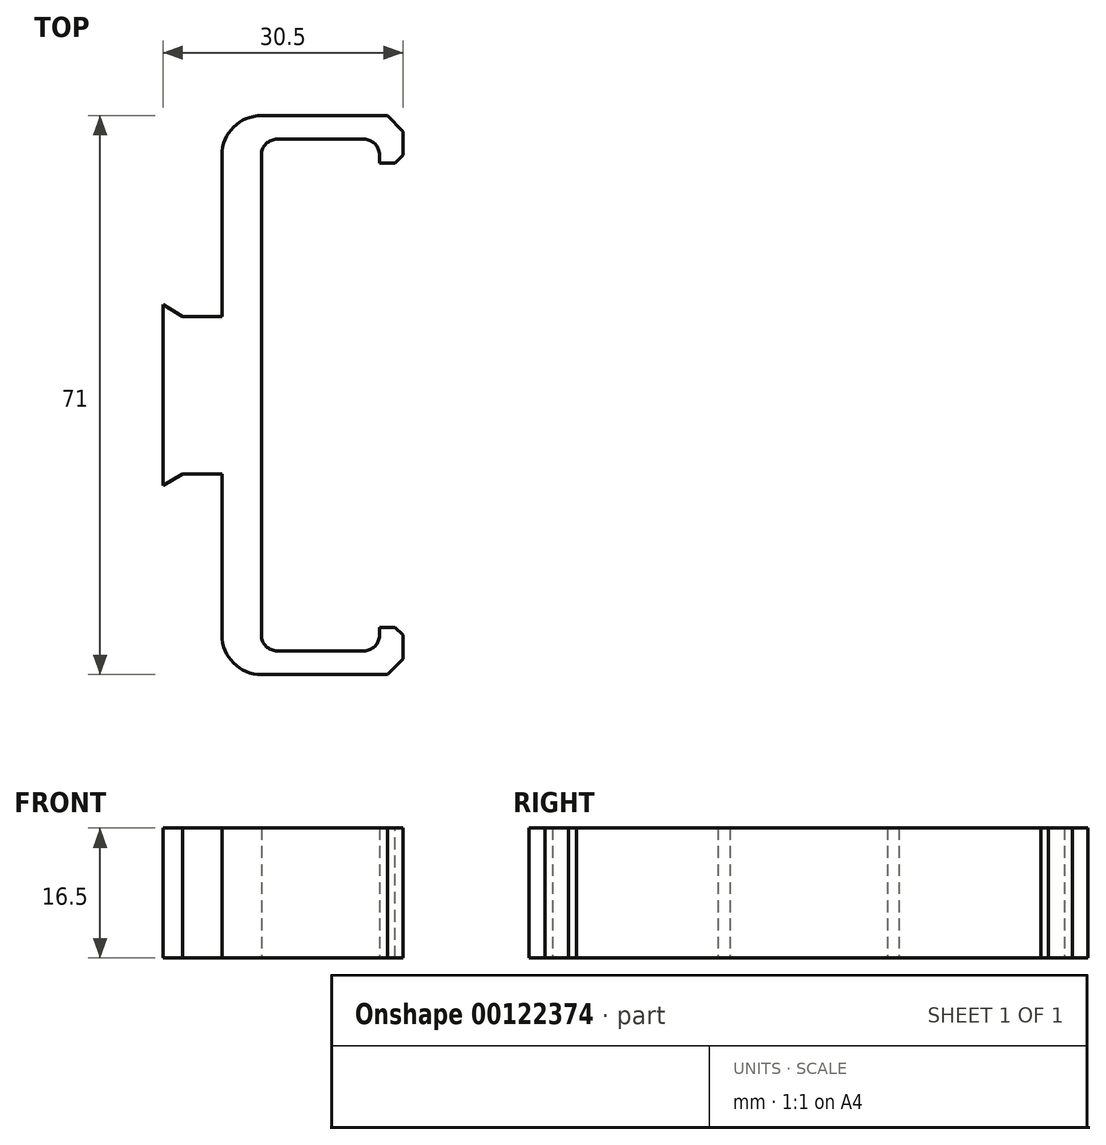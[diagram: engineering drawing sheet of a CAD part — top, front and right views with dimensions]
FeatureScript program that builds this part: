
annotation { "Feature Type Name" : "Feature", "Feature Type Description" : "" }
export const myFeature = defineFeature(function(context is Context, id is Id, definition is map)
    precondition{}
    {
        {
            var Q0;
            Q0=qCreatedBy(makeId("Top.planeOp"),FACE);
            var sketch = newSketch(context, id + "F0", { "sketchPlane" : qUnion([Q0])});
            skLineSegment(sketch, "E0.bottom", {"start": v(0, 35.5) * mm, "end": v(23, 35.5) * mm});
            skLineSegment(sketch, "E0.top", {"start": v(0, -35.5) * mm, "end": v(23, -35.5) * mm});
            skLineSegment(sketch, "E0.left", {"start": v(0, 35.5) * mm, "end": v(0, 10) * mm});
            skLineSegment(sketch, "E0.right", {"start": v(23, 35.5) * mm, "end": v(23, 29.5) * mm});
            skLineSegment(sketch, "E1.bottom", {"start": v(5, 32.5) * mm, "end": v(20, 32.5) * mm});
            skLineSegment(sketch, "E1.top", {"start": v(5, -32.5) * mm, "end": v(20, -32.5) * mm});
            skLineSegment(sketch, "E1.left", {"start": v(5, 32.5) * mm, "end": v(5, -32.5) * mm});
            skLineSegment(sketch, "E1.right", {"start": v(20, 32.5) * mm, "end": v(20, 29.5) * mm});
            skLineSegment(sketch, "E2", {"start": v(20, 29.5) * mm, "end": v(23, 29.5) * mm});
            skLineSegment(sketch, "E3", {"start": v(20, -29.5) * mm, "end": v(23, -29.5) * mm});
            skLineSegment(sketch, "E4.trimOffspring", {"start": v(20, -29.5) * mm, "end": v(20, -32.5) * mm});
            skLineSegment(sketch, "E5.trimOffspring", {"start": v(23, -29.5) * mm, "end": v(23, -35.5) * mm});
            skLineSegment(sketch, "E6.bottom", {"start": v(-5, 10) * mm, "end": v(0, 10) * mm});
            skLineSegment(sketch, "E6.top", {"start": v(-5, -10) * mm, "end": v(0, -10) * mm});
            skLineSegment(sketch, "E6.left", {"start": v(-5, 10) * mm, "end": v(-5, -10) * mm});
            skLineSegment(sketch, "E7.trimOffspring", {"start": v(0, -10) * mm, "end": v(0, -35.5) * mm});
            skSolve(sketch);
        }
        {
            var Q0;
            Q0=makeQuery(id+"F0.imprint","IMPRINT",FACE,{"disambiguationData":[TD([[makeQuery(id+"F0.imprint","IMPRINT",EDGE,{"derivedFrom":sQuery(id+"F0.wireOp",EDGE,"E0.bottom")}),-1.0]])]});
            extrude(context, id + "F1", {"entities" : qUnion([Q0]), "depth" : 16.5 * mm});
        }
        {
            var Q0;
            Q0=makeQuery(id+"F1.opExtrude","SWEPT_EDGE",EDGE,{"disambiguationData":[OSD([sQuery(id+"F0.wireOp",EDGE,"E0.top"),sQuery(id+"F0.wireOp",EDGE,"E7.trimOffspring")])]});
            var Q1;
            Q1=makeQuery(id+"F1.opExtrude","SWEPT_EDGE",EDGE,{"disambiguationData":[OSD([sQuery(id+"F0.wireOp",EDGE,"E0.bottom"),sQuery(id+"F0.wireOp",EDGE,"E0.left")])]});
            fillet(context, id + "F2", {"entities" : qUnion([Q0, Q1]), "radius" : 5 * mm, "tangentPropagation" : true, "allowEdgeOverflow" : false});
        }
        {
            var Q0;
            Q0=makeQuery(id+"F1.opExtrude","SWEPT_EDGE",EDGE,{"disambiguationData":[OSD([sQuery(id+"F0.wireOp",EDGE,"E1.bottom"),sQuery(id+"F0.wireOp",EDGE,"E1.left")])]});
            var Q1;
            Q1=makeQuery(id+"F1.opExtrude","SWEPT_EDGE",EDGE,{"disambiguationData":[OSD([sQuery(id+"F0.wireOp",EDGE,"E1.top"),sQuery(id+"F0.wireOp",EDGE,"E1.left")])]});
            var Q2;
            Q2=makeQuery(id+"F1.opExtrude","SWEPT_EDGE",EDGE,{"disambiguationData":[OSD([sQuery(id+"F0.wireOp",EDGE,"E1.bottom"),sQuery(id+"F0.wireOp",EDGE,"E1.right")])]});
            var Q3;
            Q3=makeQuery(id+"F1.opExtrude","SWEPT_EDGE",EDGE,{"disambiguationData":[OSD([sQuery(id+"F0.wireOp",EDGE,"E1.top"),sQuery(id+"F0.wireOp",EDGE,"E4.trimOffspring")])]});
            fillet(context, id + "F3", {"entities" : qUnion([Q0, Q1, Q2, Q3]), "radius" : 2 * mm, "tangentPropagation" : true, "allowEdgeOverflow" : false});
        }
        {
            var Q0;
            Q0=makeQuery(id+"F1.opExtrude","SWEPT_EDGE",EDGE,{"disambiguationData":[OSD([sQuery(id+"F0.wireOp",EDGE,"E0.right"),sQuery(id+"F0.wireOp",EDGE,"E2")])]});
            var Q1;
            Q1=makeQuery(id+"F1.opExtrude","SWEPT_EDGE",EDGE,{"disambiguationData":[OSD([sQuery(id+"F0.wireOp",EDGE,"E3"),sQuery(id+"F0.wireOp",EDGE,"E5.trimOffspring")])]});
            chamfer(context, id + "F4", {"entities" : qUnion([Q0, Q1]), "width" : 1 * mm, "tangentPropagation" : true});
        }
        {
            var Q0;
            Q0=makeQuery(id+"F1.opExtrude","SWEPT_EDGE",EDGE,{"disambiguationData":[OSD([sQuery(id+"F0.wireOp",EDGE,"E0.bottom"),sQuery(id+"F0.wireOp",EDGE,"E0.right")])]});
            var Q1;
            Q1=makeQuery(id+"F1.opExtrude","SWEPT_EDGE",EDGE,{"disambiguationData":[OSD([sQuery(id+"F0.wireOp",EDGE,"E0.top"),sQuery(id+"F0.wireOp",EDGE,"E5.trimOffspring")])]});
            chamfer(context, id + "F5", {"entities" : qUnion([Q0, Q1]), "width" : 2 * mm, "tangentPropagation" : true});
        }
        {
            var Q0;
            Q0=qCreatedBy(makeId("Top.planeOp"),FACE);
            var sketch = newSketch(context, id + "F6", { "sketchPlane" : qUnion([Q0])});
            skLineSegment(sketch, "E8", {"start": v(-7.5, 11.5) * mm, "end": v(-7.5, -11.5) * mm});
            skLineSegment(sketch, "E9", {"start": v(-7.5, -11.5) * mm, "end": v(-5, -10) * mm});
            skLineSegment(sketch, "E10", {"start": v(-5, -10) * mm, "end": v(-5, 10) * mm});
            skLineSegment(sketch, "E11", {"start": v(-5, 10) * mm, "end": v(-7.5, 11.5) * mm});
            skSolve(sketch);
        }
        {
            var Q0;
            Q0=makeQuery(id+"F6.imprint","IMPRINT",FACE,{"disambiguationData":[TD([[makeQuery(id+"F6.imprint","IMPRINT",EDGE,{"derivedFrom":sQuery(id+"F6.wireOp",EDGE,"E8")}),1.0]])]});
            var Q1;
            Q1=makeQuery(id+"F1.opExtrude","CAP_FACE",FACE,{"disambiguationData":[OSD([sQuery(id+"F0.wireOp",EDGE,"E0.bottom"),sQuery(id+"F0.wireOp",EDGE,"E0.top"),sQuery(id+"F0.wireOp",EDGE,"E0.left"),sQuery(id+"F0.wireOp",EDGE,"E0.right"),sQuery(id+"F0.wireOp",EDGE,"E1.bottom"),sQuery(id+"F0.wireOp",EDGE,"E1.top"),sQuery(id+"F0.wireOp",EDGE,"E1.left"),sQuery(id+"F0.wireOp",EDGE,"E1.right"),sQuery(id+"F0.wireOp",EDGE,"E2"),sQuery(id+"F0.wireOp",EDGE,"E3"),sQuery(id+"F0.wireOp",EDGE,"E4.trimOffspring"),sQuery(id+"F0.wireOp",EDGE,"E5.trimOffspring"),sQuery(id+"F0.wireOp",EDGE,"E6.bottom"),sQuery(id+"F0.wireOp",EDGE,"E6.top"),sQuery(id+"F0.wireOp",EDGE,"E6.left"),sQuery(id+"F0.wireOp",EDGE,"E7.trimOffspring")])],"isStart":false});
            extrude(context, id + "F7", {"entities" : qUnion([Q0]), "operationType" : NewBodyOperationType.ADD, "endBoundEntityFace" : qUnion([Q1]), "depth" : 16.5 * mm});
        }
    });
